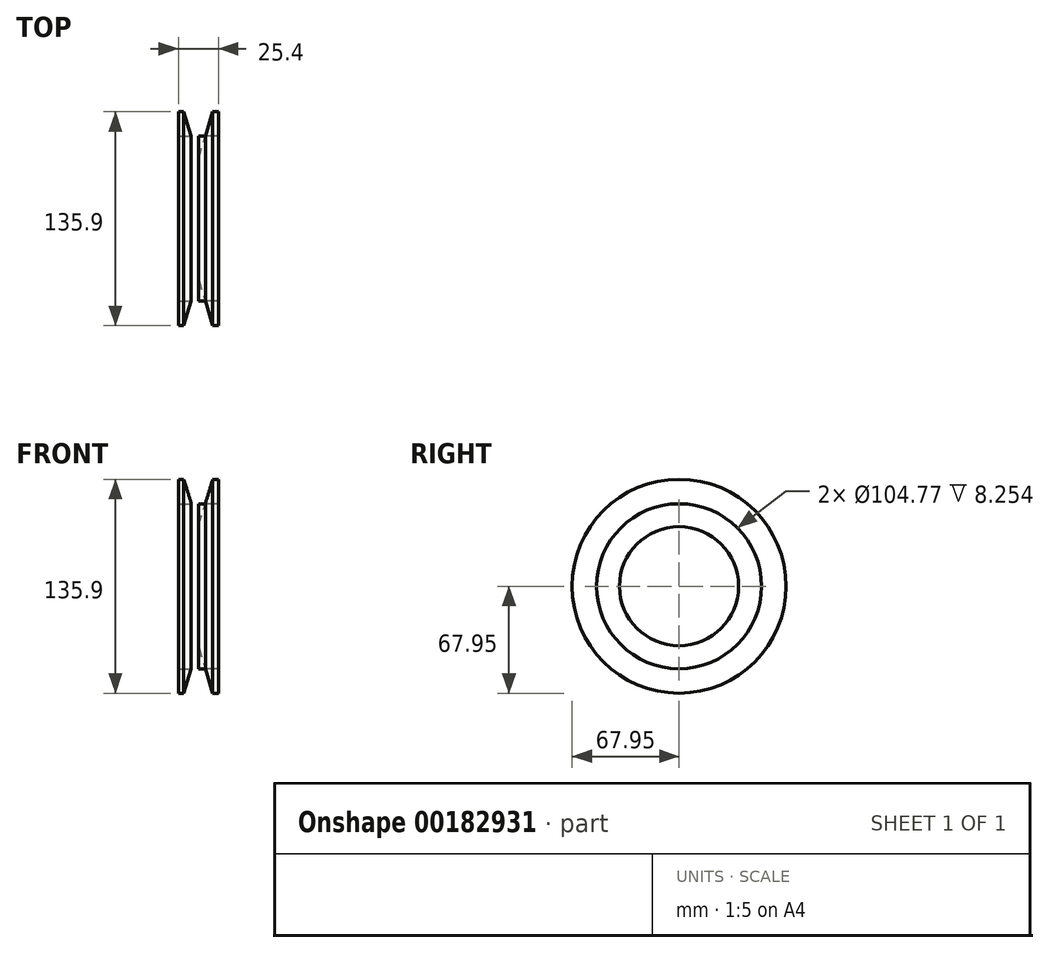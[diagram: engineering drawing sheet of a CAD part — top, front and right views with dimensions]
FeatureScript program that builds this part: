
annotation { "Feature Type Name" : "Feature", "Feature Type Description" : "" }
export const myFeature = defineFeature(function(context is Context, id is Id, definition is map)
    precondition{}
    {
        {
            var Q0;
            Q0=qCreatedBy(makeId("Front.planeOp"),FACE);
            var sketch = newSketch(context, id + "F0", { "sketchPlane" : qUnion([Q0])});
            skLineSegment(sketch, "E0", {"start": v(0, 0) * mm, "end": v(0, 52.39) * mm});
            skLineSegment(sketch, "E1.0", {"start": v(12.7, 0) * mm, "end": v(12.7, 67.94) * mm});
            skLineSegment(sketch, "E2", {"start": v(9.2, 67.95) * mm, "end": v(0, 37.85) * mm});
            skLineSegment(sketch, "E3", {"start": v(9.2, 67.94) * mm, "end": v(12.7, 67.94) * mm});
            skLineSegment(sketch, "E4.0", {"start": v(0, 52.39) * mm, "end": v(12.7, 52.39) * mm});
            skLineSegment(sketch, "E5", {"start": v(0, 37.85) * mm, "end": v(0, 0) * mm});
            skLineSegment(sketch, "E6", {"start": v(0, 0) * mm, "end": v(42.96, 0) * mm});
            skSolve(sketch);
        }
        {
            var Q0;
            {var subQ0=sQuery(id+"F0.wireOp",EDGE,"E5");Q0=makeQuery(id+"F0.imprint","IMPRINT",FACE,{"disambiguationData":[TD([[makeQuery(id+"F0.imprint","IMPRINT",EDGE,{"derivedFrom":subQ0}),1.0]])]});}
            var Q1;
            {var subQ0=sQuery(id+"F0.wireOp",EDGE,"E0");Q1=makeQuery(id+"F0.imprint","IMPRINT",FACE,{"disambiguationData":[TD([[makeQuery(id+"F0.imprint","IMPRINT",EDGE,{"derivedFrom":subQ0}),-1.0]])]});}
            var Q2;
            {var subQ0=sQuery(id+"F0.wireOp",EDGE,"E3");Q2=makeQuery(id+"F0.imprint","IMPRINT",FACE,{"disambiguationData":[TD([[makeQuery(id+"F0.imprint","IMPRINT",EDGE,{"derivedFrom":subQ0}),-1.0]])]});}
            var Q3;
            Q3=sQuery(id+"F0.wireOp",EDGE,"E6");
            revolve(context, id + "F1", {"entities" : qUnion([Q0, Q1, Q2]), "axis" : qUnion([Q3]), "revolveType" : RevolveType.FULL});
        }
        {
            var Q0;
            Q0=makeQuery(id+"F1.opRevolve","SWEPT_FACE",FACE,{"disambiguationData":[OSD([sQuery(id+"F0.wireOp",EDGE,"E0"),sQuery(id+"F0.wireOp",EDGE,"E5")])]});
            var sketch = newSketch(context, id + "F2", { "sketchPlane" : qUnion([Q0])});
            skCircle(sketch, "E7", {"center": v(0, 0) * mm, "radius": 17.5 * mm});
            skSolve(sketch);
        }
        {
            var Q0;
            Q0 = qSketchRegion(id + "F2", true);
            extrude(context, id + "F3", {"entities" : qUnion([Q0]), "operationType" : NewBodyOperationType.REMOVE, "oppositeDirection" : true, "depth" : 25 * mm});
        }
        {
            var Q0;
            Q0=makeQuery(id+"F1.opRevolve","SWEPT_BODY",BODY,{"disambiguationData":[OSD([sQuery(id+"F0.wireOp",EDGE,"E0"),sQuery(id+"F0.wireOp",EDGE,"E1.0"),sQuery(id+"F0.wireOp",EDGE,"E2"),sQuery(id+"F0.wireOp",EDGE,"E3"),sQuery(id+"F0.wireOp",EDGE,"E4.0"),sQuery(id+"F0.wireOp",EDGE,"E5"),sQuery(id+"F0.wireOp",EDGE,"E6")])]});
            var Q1;
            Q1=qCreatedBy(makeId("Right.planeOp"),FACE);
            mirror(context, id + "F4", {"operationType" : NewBodyOperationType.ADD, "entities" : qUnion([Q0]), "mirrorPlane" : qUnion([Q1])});
        }
    });
